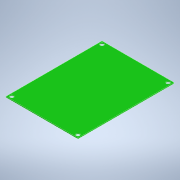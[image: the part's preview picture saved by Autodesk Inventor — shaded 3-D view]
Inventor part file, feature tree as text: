
AUTODESK INVENTOR PART (.ipt)
format: ipt  version: 2022 (Build 260153000, 153)  size: 3,005,952 bytes
history: native  units: in
note: dims shown in document units (in); Inventor stores cm internally (conversion verified against a paired STEP export)
features: extrude x2, sketch x2, hole x1
ambient origin geometry x8: Origin, YZ Plane, XZ Plane, XY Plane, X Axis, Y Axis, Z Axis, Center Point
bodies: Solid1 (feature_tree)
feature tree (5):
  extrude  "Extrusion1"  Depth=2.2638in
  hole  "Hole2"  [1 undecoded]
  extrude  "Extrusion4"  Depth=0.0118in
  sketch  "Sketch1"  dims[d0=1.6969in d1=2.2638in]
  sketch  "Sketch6"  dims[d2=0.0197in d3=0.0in d37=0.0866in d38=0.2726in d39=0.1732in d40=0.0787in d41=90.0deg d42=0.315in d43=0.8108in d57=0.0039in d58=0.0118in d59=0.128in d60=0.126in d61=27.9528in d63=0.0098in d64=0.3937in d66=0.3937in d68=0.0118in d69=0.0039in d70=0.0049in d71=0.003in d72=27.9528in d74=0.0098in d75=0.3937in d77=0.3937in d79=0.002in d80=0.0in d81=0.7874in d83=0.8504in d84=0.3937in d86=0.3937in d88=0.7874in d90=360.0deg d92=0.0689in d93=0.0689in d94=0.0689in d95=0.0689in]
note: 1 required parameter value undecoded (feature->parameter linkage not recoverable at this tier; creation-order binding heuristic only, values carry confidence <= 0.55)
